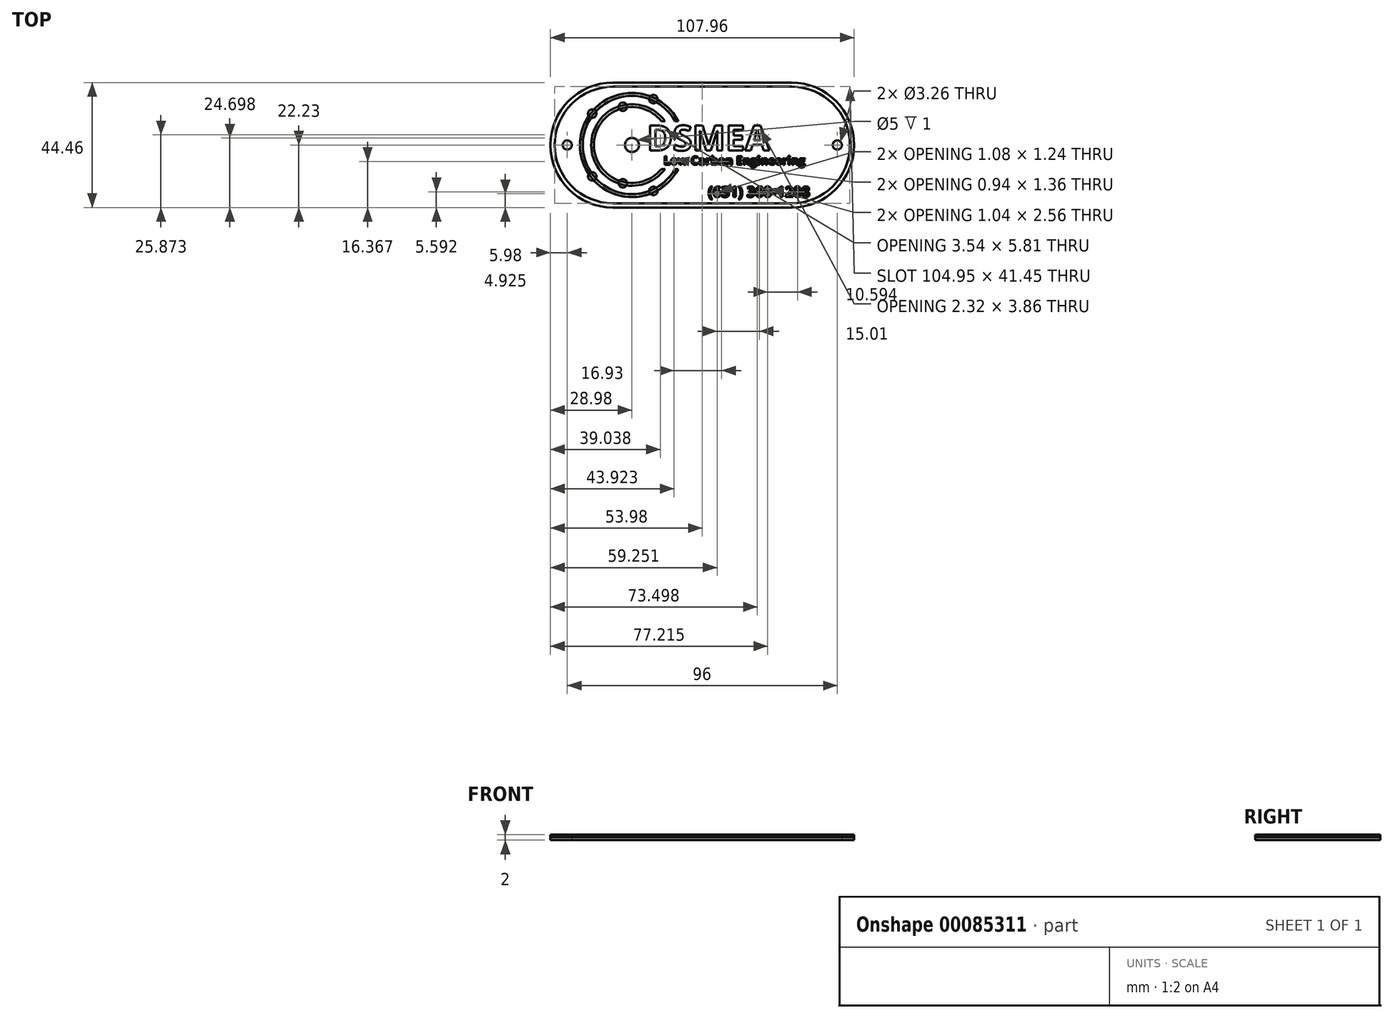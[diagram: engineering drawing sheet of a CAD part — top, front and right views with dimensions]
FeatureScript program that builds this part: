
annotation { "Feature Type Name" : "Feature", "Feature Type Description" : "" }
export const myFeature = defineFeature(function(context is Context, id is Id, definition is map)
    precondition{}
    {
        {
            var Q0;
            Q0=qCreatedBy(makeId("Top.planeOp"),FACE);
            var sketch = newSketch(context, id + "F0", { "sketchPlane" : qUnion([Q0])});
            skLineSegment(sketch, "E0.bottom", {"start": v(31.75, 22.22) * mm, "end": v(-31.75, 22.22) * mm});
            skLineSegment(sketch, "E0.top", {"start": v(31.75, -22.23) * mm, "end": v(-31.75, -22.23) * mm});
            skPoint(sketch, "E0.middle", {"position": v(0, 0) * mm});
            skArc(sketch, "E1", {"start": v(31.75, -22.23) * mm, "mid": v(53.98, 0) * mm, "end": v(31.75, 22.23) * mm});
            skArc(sketch, "E2", {"start": v(-31.75, 22.23) * mm, "mid": v(-53.98, 0) * mm, "end": v(-31.75, -22.23) * mm});
            skSolve(sketch);
        }
        {
            var Q0;
            Q0=qSketchRegion(id+"F0",true);
            extrude(context, id + "F1", {"entities" : qUnion([Q0]), "depth" : 2 * mm});
        }
        {
            var Q0;
            Q0=qCreatedBy(makeId("Top.planeOp"),FACE);
            cPlane(context, id + "F2", {"entities" : qUnion([Q0]), "cplaneType" : CPlaneType.OFFSET, "offset" : 1 * mm, "width" : 150 * mm, "height" : 150 * mm});
        }
        {
            var Q0;
            Q0=qCreatedBy(id+"F2.planeOp",FACE);
            var sketch = newSketch(context, id + "F3", { "sketchPlane" : qUnion([Q0])});
            skArc(sketch, "E3", {"start": v(-31.75, 22.23) * mm, "mid": v(-53.98, 0) * mm, "end": v(-31.75, -22.23) * mm});
            skArc(sketch, "E4.0", {"start": v(-31.75, 20.73) * mm, "mid": v(-52.48, 0) * mm, "end": v(-31.75, -20.73) * mm});
            skArc(sketch, "E5.MirrorC", {"start": v(31.75, 22.23) * mm, "mid": v(53.98, 0) * mm, "end": v(31.75, -22.23) * mm});
            skArc(sketch, "E6.MirrorC", {"start": v(31.75, 20.73) * mm, "mid": v(52.48, 0) * mm, "end": v(31.75, -20.73) * mm});
            skLineSegment(sketch, "E7", {"start": v(-31.75, -22.23) * mm, "end": v(31.75, -22.23) * mm});
            skLineSegment(sketch, "E8.MirrorCS", {"start": v(-31.75, 22.23) * mm, "end": v(31.75, 22.23) * mm});
            skLineSegment(sketch, "E9.0", {"start": v(-31.75, 20.73) * mm, "end": v(31.75, 20.73) * mm});
            skLineSegment(sketch, "E10.MirrorCS", {"start": v(-31.75, -20.73) * mm, "end": v(31.75, -20.73) * mm});
            skSolve(sketch);
        }
        {
            var Q0;
            Q0=qSketchRegion(id+"F3",true);
            extrude(context, id + "F4", {"entities" : qUnion([Q0]), "depth" : 1 * mm});
        }
        {
            var Q0;
            Q0=qCreatedBy(id+"F2.planeOp",FACE);
            var sketch = newSketch(context, id + "F5", { "sketchPlane" : qUnion([Q0])});
            skArc(sketch, "E11", {"start": v(-8.57, 8.5) * mm, "mid": v(-43.5, 0) * mm, "end": v(-8.57, -8.5) * mm});
            skArc(sketch, "E12", {"start": v(-9.7, 8.5) * mm, "mid": v(-42.5, 0) * mm, "end": v(-9.7, -8.5) * mm});
            skLineSegment(sketch, "E13.bottom", {"start": v(-8.57, 8.5) * mm, "end": v(-9.7, 8.5) * mm});
            skLineSegment(sketch, "E13.top", {"start": v(-8.57, -8.5) * mm, "end": v(-9.7, -8.5) * mm});
            skPoint(sketch, "E13.middle", {"position": v(0, 0) * mm});
            skSolve(sketch);
        }
        {
            var Q0;
            Q0=qSketchRegion(id+"F5",true);
            extrude(context, id + "F6", {"entities" : qUnion([Q0]), "depth" : 1 * mm});
        }
        {
            var Q0;
            Q0=qCreatedBy(id+"F2.planeOp",FACE);
            var sketch = newSketch(context, id + "F7", { "sketchPlane" : qUnion([Q0])});
            skArc(sketch, "E14", {"start": v(-13.25, 8.5) * mm, "mid": v(-39.5, 0) * mm, "end": v(-13.25, -8.5) * mm});
            skArc(sketch, "E15", {"start": v(-14.51, 8.5) * mm, "mid": v(-38.5, 0) * mm, "end": v(-14.51, -8.5) * mm});
            skLineSegment(sketch, "E16.bottom", {"start": v(-13.25, 8.5) * mm, "end": v(-14.51, 8.5) * mm});
            skLineSegment(sketch, "E16.top", {"start": v(-13.25, -8.5) * mm, "end": v(-14.51, -8.5) * mm});
            skPoint(sketch, "E16.middle", {"position": v(0, 0) * mm});
            skSolve(sketch);
        }
        {
            var Q0;
            Q0=qSketchRegion(id+"F7",true);
            extrude(context, id + "F8", {"entities" : qUnion([Q0]), "depth" : 1 * mm});
        }
        {
            var Q0;
            Q0=qCreatedBy(id+"F2.planeOp",FACE);
            var sketch = newSketch(context, id + "F9", { "sketchPlane" : qUnion([Q0])});
            skCircle(sketch, "E17", {"center": v(-25, 0) * mm, "radius": 2.5 * mm});
            skCircle(sketch, "E18", {"center": v(-17.4, 16.31) * mm, "radius": 1.5 * mm});
            skLineSegment(sketch, "E19.anchor1", {"start": v(-25, 0) * mm, "end": v(-17.4, 16.31) * mm, "construction": true});
            skLineSegment(sketch, "E19.anchor2", {"start": v(-25, 0) * mm, "end": v(-17.4, -16.31) * mm, "construction": true});
            skCircle(sketch, "E20", {"center": v(-28.23, 13.62) * mm, "radius": 1.5 * mm});
            skCircle(sketch, "E21.MirrorC", {"center": v(-28.23, -13.62) * mm, "radius": 1.5 * mm});
            skLineSegment(sketch, "E22", {"start": v(-59.58, 0) * mm, "end": v(0, 0) * mm, "construction": true});
            skCircle(sketch, "E23", {"center": v(-25, 0) * mm, "radius": 18 * mm, "construction": true});
            skCircle(sketch, "E24", {"center": v(-25, 0) * mm, "radius": 14 * mm, "construction": true});
            skLineSegment(sketch, "E25", {"start": v(-28.23, 13.62) * mm, "end": v(-35.98, 8.68) * mm, "construction": true});
            skLineSegment(sketch, "E26", {"start": v(-28.23, 13.62) * mm, "end": v(-19.08, 12.69) * mm, "construction": true});
            skCircle(sketch, "E27.1.0", {"center": v(-39.12, 11.16) * mm, "radius": 1.5 * mm});
            skCircle(sketch, "E27.2.0", {"center": v(-39.12, -11.16) * mm, "radius": 1.5 * mm});
            skCircle(sketch, "E27.3.0", {"center": v(-17.4, -16.31) * mm, "radius": 1.5 * mm});
            skSolve(sketch);
        }
        {
            var Q0;
            Q0=qSketchRegion(id+"F9",true);
            extrude(context, id + "F10", {"entities" : qUnion([Q0]), "depth" : 1 * mm});
        }
        {
            var Q0;
            Q0=qCreatedBy(id+"F2.planeOp",FACE);
            var sketch = newSketch(context, id + "F11", { "sketchPlane" : qUnion([Q0])});
            skText(sketch, "E28", { "text": "DSMEA", "fontName": "OpenSans-Bold.ttf"});
            const initialGuessF11  = {"E28": [-0.01973, -0.002, 1, 0, 0.009]};
            skSetInitialGuess(sketch, initialGuessF11);
            skSolve(sketch);
        }
        {
            var Q0;
            Q0=qSketchRegion(id+"F11",true);
            extrude(context, id + "F12", {"entities" : qUnion([Q0]), "depth" : 1 * mm});
        }
        {
            var Q0;
            Q0=qCreatedBy(id+"F2.planeOp",FACE);
            var sketch = newSketch(context, id + "F13", { "sketchPlane" : qUnion([Q0])});
            skText(sketch, "E29", { "text": "Low Carbon Engineering", "fontName": "OpenSans-Bold.ttf"});
            const initialGuessF13  = {"E29": [-0.0137, -0.007, 1, 0, 0.003]};
            skSetInitialGuess(sketch, initialGuessF13);
            skSolve(sketch);
        }
        {
            var Q0;
            Q0=qSketchRegion(id+"F13",true);
            extrude(context, id + "F14", {"entities" : qUnion([Q0]), "depth" : 1 * mm});
        }
        {
            var Q0;
            Q0=qCreatedBy(id+"F2.planeOp",FACE);
            var sketch = newSketch(context, id + "F15", { "sketchPlane" : qUnion([Q0])});
            skText(sketch, "E30", { "text": "(631) 360-1208", "fontName": "OpenSans-Bold.ttf"});
            const initialGuessF15  = {"E30": [0.002, -0.0185, 1, 0, 0.00375]};
            skSetInitialGuess(sketch, initialGuessF15);
            skSolve(sketch);
        }
        {
            var Q0;
            Q0=qSketchRegion(id+"F15",true);
            extrude(context, id + "F16", {"entities" : qUnion([Q0]), "depth" : 1 * mm});
        }
        {
            var Q0;
            Q0=makeQuery(id+"F6.opExtrude","SWEPT_BODY",BODY,{"disambiguationData":[OSD([sQuery(id+"F5.wireOp",EDGE,"E11"),sQuery(id+"F5.wireOp",EDGE,"E12")])]});
            var Q1;
            Q1=makeQuery(id+"F1.opExtrude","SWEPT_BODY",BODY,{"disambiguationData":[OSD([sQuery(id+"F0.wireOp",EDGE,"E0.bottom"),sQuery(id+"F0.wireOp",EDGE,"E0.top"),sQuery(id+"F0.wireOp",EDGE,"E1"),sQuery(id+"F0.wireOp",EDGE,"E2")])]});
            booleanBodies(context, id + "F17", {"operationType" : BooleanOperationType.SUBTRACTION, "tools" : qUnion([Q0]), "targets" : qUnion([Q1]), "keepTools" : true});
        }
        {
            var Q0;
            Q0=makeQuery(id+"F6.opExtrude","SWEPT_BODY",BODY,{"disambiguationData":[OSD([sQuery(id+"F5.wireOp",EDGE,"E11"),sQuery(id+"F5.wireOp",EDGE,"E12")])]});
            var Q1;
            Q1=makeQuery(id+"F10.opExtrude","SWEPT_BODY",BODY,{"disambiguationData":[OSD([sQuery(id+"F9.wireOp",EDGE,"E17")])]});
            var Q2;
            Q2=makeQuery(id+"F8.opExtrude","SWEPT_BODY",BODY,{"disambiguationData":[OSD([sQuery(id+"F7.wireOp",EDGE,"E14"),sQuery(id+"F7.wireOp",EDGE,"E15")])]});
            var Q3;
            Q3=makeQuery(id+"F1.opExtrude","SWEPT_BODY",BODY,{"disambiguationData":[OSD([sQuery(id+"F0.wireOp",EDGE,"E0.bottom"),sQuery(id+"F0.wireOp",EDGE,"E0.top"),sQuery(id+"F0.wireOp",EDGE,"E1"),sQuery(id+"F0.wireOp",EDGE,"E2")])]});
            booleanBodies(context, id + "F18", {"operationType" : BooleanOperationType.SUBTRACTION, "tools" : qUnion([Q0, Q1, Q2]), "targets" : qUnion([Q3]), "keepTools" : true});
        }
        {
            var Q0;
            Q0=makeQuery(id+"F12.opExtrude","SWEPT_BODY",BODY,{"disambiguationData":[OSD([sQuery(id+"F11.wireOp",EDGE,"E28.sketch_text.stroke-0"),sQuery(id+"F11.wireOp",EDGE,"E28.sketch_text.stroke-1"),sQuery(id+"F11.wireOp",EDGE,"E28.sketch_text.stroke-2"),sQuery(id+"F11.wireOp",EDGE,"E28.sketch_text.stroke-3"),sQuery(id+"F11.wireOp",EDGE,"E28.sketch_text.stroke-4"),sQuery(id+"F11.wireOp",EDGE,"E28.sketch_text.stroke-5"),sQuery(id+"F11.wireOp",EDGE,"E28.sketch_text.stroke-6"),sQuery(id+"F11.wireOp",EDGE,"E28.sketch_text.stroke-7"),sQuery(id+"F11.wireOp",EDGE,"E28.sketch_text.stroke-8"),sQuery(id+"F11.wireOp",EDGE,"E28.sketch_text.stroke-9"),sQuery(id+"F11.wireOp",EDGE,"E28.sketch_text.stroke-10"),sQuery(id+"F11.wireOp",EDGE,"E28.sketch_text.stroke-11")])]});
            var Q1;
            Q1=makeQuery(id+"F12.opExtrude","SWEPT_BODY",BODY,{"disambiguationData":[OSD([sQuery(id+"F11.wireOp",EDGE,"E28.sketch_text.stroke-12"),sQuery(id+"F11.wireOp",EDGE,"E28.sketch_text.stroke-13"),sQuery(id+"F11.wireOp",EDGE,"E28.sketch_text.stroke-14"),sQuery(id+"F11.wireOp",EDGE,"E28.sketch_text.stroke-15"),sQuery(id+"F11.wireOp",EDGE,"E28.sketch_text.stroke-16"),sQuery(id+"F11.wireOp",EDGE,"E28.sketch_text.stroke-17"),sQuery(id+"F11.wireOp",EDGE,"E28.sketch_text.stroke-18"),sQuery(id+"F11.wireOp",EDGE,"E28.sketch_text.stroke-19"),sQuery(id+"F11.wireOp",EDGE,"E28.sketch_text.stroke-20"),sQuery(id+"F11.wireOp",EDGE,"E28.sketch_text.stroke-21"),sQuery(id+"F11.wireOp",EDGE,"E28.sketch_text.stroke-22"),sQuery(id+"F11.wireOp",EDGE,"E28.sketch_text.stroke-23"),sQuery(id+"F11.wireOp",EDGE,"E28.sketch_text.stroke-24"),sQuery(id+"F11.wireOp",EDGE,"E28.sketch_text.stroke-25"),sQuery(id+"F11.wireOp",EDGE,"E28.sketch_text.stroke-26"),sQuery(id+"F11.wireOp",EDGE,"E28.sketch_text.stroke-27"),sQuery(id+"F11.wireOp",EDGE,"E28.sketch_text.stroke-28"),sQuery(id+"F11.wireOp",EDGE,"E28.sketch_text.stroke-29"),sQuery(id+"F11.wireOp",EDGE,"E28.sketch_text.stroke-30"),sQuery(id+"F11.wireOp",EDGE,"E28.sketch_text.stroke-31"),sQuery(id+"F11.wireOp",EDGE,"E28.sketch_text.stroke-32"),sQuery(id+"F11.wireOp",EDGE,"E28.sketch_text.stroke-33"),sQuery(id+"F11.wireOp",EDGE,"E28.sketch_text.stroke-34"),sQuery(id+"F11.wireOp",EDGE,"E28.sketch_text.stroke-35"),sQuery(id+"F11.wireOp",EDGE,"E28.sketch_text.stroke-36"),sQuery(id+"F11.wireOp",EDGE,"E28.sketch_text.stroke-37"),sQuery(id+"F11.wireOp",EDGE,"E28.sketch_text.stroke-38"),sQuery(id+"F11.wireOp",EDGE,"E28.sketch_text.stroke-39")])]});
            var Q2;
            Q2=makeQuery(id+"F12.opExtrude","SWEPT_BODY",BODY,{"disambiguationData":[OSD([sQuery(id+"F11.wireOp",EDGE,"E28.sketch_text.stroke-40"),sQuery(id+"F11.wireOp",EDGE,"E28.sketch_text.stroke-41"),sQuery(id+"F11.wireOp",EDGE,"E28.sketch_text.stroke-42"),sQuery(id+"F11.wireOp",EDGE,"E28.sketch_text.stroke-43"),sQuery(id+"F11.wireOp",EDGE,"E28.sketch_text.stroke-44"),sQuery(id+"F11.wireOp",EDGE,"E28.sketch_text.stroke-45"),sQuery(id+"F11.wireOp",EDGE,"E28.sketch_text.stroke-46"),sQuery(id+"F11.wireOp",EDGE,"E28.sketch_text.stroke-47"),sQuery(id+"F11.wireOp",EDGE,"E28.sketch_text.stroke-48"),sQuery(id+"F11.wireOp",EDGE,"E28.sketch_text.stroke-49"),sQuery(id+"F11.wireOp",EDGE,"E28.sketch_text.stroke-50"),sQuery(id+"F11.wireOp",EDGE,"E28.sketch_text.stroke-51"),sQuery(id+"F11.wireOp",EDGE,"E28.sketch_text.stroke-52"),sQuery(id+"F11.wireOp",EDGE,"E28.sketch_text.stroke-53"),sQuery(id+"F11.wireOp",EDGE,"E28.sketch_text.stroke-54"),sQuery(id+"F11.wireOp",EDGE,"E28.sketch_text.stroke-55"),sQuery(id+"F11.wireOp",EDGE,"E28.sketch_text.stroke-56"),sQuery(id+"F11.wireOp",EDGE,"E28.sketch_text.stroke-57"),sQuery(id+"F11.wireOp",EDGE,"E28.sketch_text.stroke-58")])]});
            var Q3;
            Q3=makeQuery(id+"F12.opExtrude","SWEPT_BODY",BODY,{"disambiguationData":[OSD([sQuery(id+"F11.wireOp",EDGE,"E28.sketch_text.stroke-59"),sQuery(id+"F11.wireOp",EDGE,"E28.sketch_text.stroke-60"),sQuery(id+"F11.wireOp",EDGE,"E28.sketch_text.stroke-61"),sQuery(id+"F11.wireOp",EDGE,"E28.sketch_text.stroke-62"),sQuery(id+"F11.wireOp",EDGE,"E28.sketch_text.stroke-63"),sQuery(id+"F11.wireOp",EDGE,"E28.sketch_text.stroke-64"),sQuery(id+"F11.wireOp",EDGE,"E28.sketch_text.stroke-65"),sQuery(id+"F11.wireOp",EDGE,"E28.sketch_text.stroke-66"),sQuery(id+"F11.wireOp",EDGE,"E28.sketch_text.stroke-67"),sQuery(id+"F11.wireOp",EDGE,"E28.sketch_text.stroke-68"),sQuery(id+"F11.wireOp",EDGE,"E28.sketch_text.stroke-69"),sQuery(id+"F11.wireOp",EDGE,"E28.sketch_text.stroke-70")])]});
            var Q4;
            Q4=makeQuery(id+"F12.opExtrude","SWEPT_BODY",BODY,{"disambiguationData":[OSD([sQuery(id+"F11.wireOp",EDGE,"E28.sketch_text.stroke-71"),sQuery(id+"F11.wireOp",EDGE,"E28.sketch_text.stroke-72"),sQuery(id+"F11.wireOp",EDGE,"E28.sketch_text.stroke-73"),sQuery(id+"F11.wireOp",EDGE,"E28.sketch_text.stroke-74"),sQuery(id+"F11.wireOp",EDGE,"E28.sketch_text.stroke-75"),sQuery(id+"F11.wireOp",EDGE,"E28.sketch_text.stroke-76"),sQuery(id+"F11.wireOp",EDGE,"E28.sketch_text.stroke-77"),sQuery(id+"F11.wireOp",EDGE,"E28.sketch_text.stroke-78"),sQuery(id+"F11.wireOp",EDGE,"E28.sketch_text.stroke-79"),sQuery(id+"F11.wireOp",EDGE,"E28.sketch_text.stroke-80"),sQuery(id+"F11.wireOp",EDGE,"E28.sketch_text.stroke-81"),sQuery(id+"F11.wireOp",EDGE,"E28.sketch_text.stroke-82")])]});
            var Q5;
            Q5=makeQuery(id+"F1.opExtrude","SWEPT_BODY",BODY,{"disambiguationData":[OSD([sQuery(id+"F0.wireOp",EDGE,"E0.bottom"),sQuery(id+"F0.wireOp",EDGE,"E0.top"),sQuery(id+"F0.wireOp",EDGE,"E1"),sQuery(id+"F0.wireOp",EDGE,"E2")])]});
            booleanBodies(context, id + "F19", {"operationType" : BooleanOperationType.SUBTRACTION, "tools" : qUnion([Q0, Q1, Q2, Q3, Q4]), "targets" : qUnion([Q5]), "keepTools" : true});
        }
        {
            var Q0;
            Q0=makeQuery(id+"F14.opExtrude","SWEPT_BODY",BODY,{"disambiguationData":[OSD([sQuery(id+"F13.wireOp",EDGE,"E29.sketch_text.stroke-0"),sQuery(id+"F13.wireOp",EDGE,"E29.sketch_text.stroke-1"),sQuery(id+"F13.wireOp",EDGE,"E29.sketch_text.stroke-2"),sQuery(id+"F13.wireOp",EDGE,"E29.sketch_text.stroke-3"),sQuery(id+"F13.wireOp",EDGE,"E29.sketch_text.stroke-4"),sQuery(id+"F13.wireOp",EDGE,"E29.sketch_text.stroke-5")])]});
            var Q1;
            Q1=makeQuery(id+"F14.opExtrude","SWEPT_BODY",BODY,{"disambiguationData":[OSD([sQuery(id+"F13.wireOp",EDGE,"E29.sketch_text.stroke-6"),sQuery(id+"F13.wireOp",EDGE,"E29.sketch_text.stroke-7"),sQuery(id+"F13.wireOp",EDGE,"E29.sketch_text.stroke-8"),sQuery(id+"F13.wireOp",EDGE,"E29.sketch_text.stroke-9"),sQuery(id+"F13.wireOp",EDGE,"E29.sketch_text.stroke-10"),sQuery(id+"F13.wireOp",EDGE,"E29.sketch_text.stroke-11"),sQuery(id+"F13.wireOp",EDGE,"E29.sketch_text.stroke-12"),sQuery(id+"F13.wireOp",EDGE,"E29.sketch_text.stroke-13"),sQuery(id+"F13.wireOp",EDGE,"E29.sketch_text.stroke-14"),sQuery(id+"F13.wireOp",EDGE,"E29.sketch_text.stroke-15"),sQuery(id+"F13.wireOp",EDGE,"E29.sketch_text.stroke-16"),sQuery(id+"F13.wireOp",EDGE,"E29.sketch_text.stroke-17"),sQuery(id+"F13.wireOp",EDGE,"E29.sketch_text.stroke-18"),sQuery(id+"F13.wireOp",EDGE,"E29.sketch_text.stroke-19"),sQuery(id+"F13.wireOp",EDGE,"E29.sketch_text.stroke-20"),sQuery(id+"F13.wireOp",EDGE,"E29.sketch_text.stroke-21"),sQuery(id+"F13.wireOp",EDGE,"E29.sketch_text.stroke-22"),sQuery(id+"F13.wireOp",EDGE,"E29.sketch_text.stroke-23")])]});
            var Q2;
            Q2=makeQuery(id+"F14.opExtrude","SWEPT_BODY",BODY,{"disambiguationData":[OSD([sQuery(id+"F13.wireOp",EDGE,"E29.sketch_text.stroke-24"),sQuery(id+"F13.wireOp",EDGE,"E29.sketch_text.stroke-25"),sQuery(id+"F13.wireOp",EDGE,"E29.sketch_text.stroke-26"),sQuery(id+"F13.wireOp",EDGE,"E29.sketch_text.stroke-27"),sQuery(id+"F13.wireOp",EDGE,"E29.sketch_text.stroke-28"),sQuery(id+"F13.wireOp",EDGE,"E29.sketch_text.stroke-29"),sQuery(id+"F13.wireOp",EDGE,"E29.sketch_text.stroke-30"),sQuery(id+"F13.wireOp",EDGE,"E29.sketch_text.stroke-31"),sQuery(id+"F13.wireOp",EDGE,"E29.sketch_text.stroke-32"),sQuery(id+"F13.wireOp",EDGE,"E29.sketch_text.stroke-33"),sQuery(id+"F13.wireOp",EDGE,"E29.sketch_text.stroke-34"),sQuery(id+"F13.wireOp",EDGE,"E29.sketch_text.stroke-35"),sQuery(id+"F13.wireOp",EDGE,"E29.sketch_text.stroke-36"),sQuery(id+"F13.wireOp",EDGE,"E29.sketch_text.stroke-37"),sQuery(id+"F13.wireOp",EDGE,"E29.sketch_text.stroke-38"),sQuery(id+"F13.wireOp",EDGE,"E29.sketch_text.stroke-39"),sQuery(id+"F13.wireOp",EDGE,"E29.sketch_text.stroke-40"),sQuery(id+"F13.wireOp",EDGE,"E29.sketch_text.stroke-41"),sQuery(id+"F13.wireOp",EDGE,"E29.sketch_text.stroke-42"),sQuery(id+"F13.wireOp",EDGE,"E29.sketch_text.stroke-43"),sQuery(id+"F13.wireOp",EDGE,"E29.sketch_text.stroke-44"),sQuery(id+"F13.wireOp",EDGE,"E29.sketch_text.stroke-45"),sQuery(id+"F13.wireOp",EDGE,"E29.sketch_text.stroke-46"),sQuery(id+"F13.wireOp",EDGE,"E29.sketch_text.stroke-47"),sQuery(id+"F13.wireOp",EDGE,"E29.sketch_text.stroke-48"),sQuery(id+"F13.wireOp",EDGE,"E29.sketch_text.stroke-49")])]});
            var Q3;
            Q3=makeQuery(id+"F14.opExtrude","SWEPT_BODY",BODY,{"disambiguationData":[OSD([sQuery(id+"F13.wireOp",EDGE,"E29.sketch_text.stroke-50"),sQuery(id+"F13.wireOp",EDGE,"E29.sketch_text.stroke-51"),sQuery(id+"F13.wireOp",EDGE,"E29.sketch_text.stroke-52"),sQuery(id+"F13.wireOp",EDGE,"E29.sketch_text.stroke-53"),sQuery(id+"F13.wireOp",EDGE,"E29.sketch_text.stroke-54"),sQuery(id+"F13.wireOp",EDGE,"E29.sketch_text.stroke-55"),sQuery(id+"F13.wireOp",EDGE,"E29.sketch_text.stroke-56"),sQuery(id+"F13.wireOp",EDGE,"E29.sketch_text.stroke-57"),sQuery(id+"F13.wireOp",EDGE,"E29.sketch_text.stroke-58"),sQuery(id+"F13.wireOp",EDGE,"E29.sketch_text.stroke-59"),sQuery(id+"F13.wireOp",EDGE,"E29.sketch_text.stroke-60"),sQuery(id+"F13.wireOp",EDGE,"E29.sketch_text.stroke-61"),sQuery(id+"F13.wireOp",EDGE,"E29.sketch_text.stroke-62"),sQuery(id+"F13.wireOp",EDGE,"E29.sketch_text.stroke-63"),sQuery(id+"F13.wireOp",EDGE,"E29.sketch_text.stroke-64")])]});
            var Q4;
            Q4=makeQuery(id+"F14.opExtrude","SWEPT_BODY",BODY,{"disambiguationData":[OSD([sQuery(id+"F13.wireOp",EDGE,"E29.sketch_text.stroke-65"),sQuery(id+"F13.wireOp",EDGE,"E29.sketch_text.stroke-66"),sQuery(id+"F13.wireOp",EDGE,"E29.sketch_text.stroke-67"),sQuery(id+"F13.wireOp",EDGE,"E29.sketch_text.stroke-68"),sQuery(id+"F13.wireOp",EDGE,"E29.sketch_text.stroke-69"),sQuery(id+"F13.wireOp",EDGE,"E29.sketch_text.stroke-70"),sQuery(id+"F13.wireOp",EDGE,"E29.sketch_text.stroke-71"),sQuery(id+"F13.wireOp",EDGE,"E29.sketch_text.stroke-72"),sQuery(id+"F13.wireOp",EDGE,"E29.sketch_text.stroke-73"),sQuery(id+"F13.wireOp",EDGE,"E29.sketch_text.stroke-74"),sQuery(id+"F13.wireOp",EDGE,"E29.sketch_text.stroke-75"),sQuery(id+"F13.wireOp",EDGE,"E29.sketch_text.stroke-76"),sQuery(id+"F13.wireOp",EDGE,"E29.sketch_text.stroke-77"),sQuery(id+"F13.wireOp",EDGE,"E29.sketch_text.stroke-78"),sQuery(id+"F13.wireOp",EDGE,"E29.sketch_text.stroke-79"),sQuery(id+"F13.wireOp",EDGE,"E29.sketch_text.stroke-80"),sQuery(id+"F13.wireOp",EDGE,"E29.sketch_text.stroke-81"),sQuery(id+"F13.wireOp",EDGE,"E29.sketch_text.stroke-82"),sQuery(id+"F13.wireOp",EDGE,"E29.sketch_text.stroke-83"),sQuery(id+"F13.wireOp",EDGE,"E29.sketch_text.stroke-84"),sQuery(id+"F13.wireOp",EDGE,"E29.sketch_text.stroke-85"),sQuery(id+"F13.wireOp",EDGE,"E29.sketch_text.stroke-86"),sQuery(id+"F13.wireOp",EDGE,"E29.sketch_text.stroke-87"),sQuery(id+"F13.wireOp",EDGE,"E29.sketch_text.stroke-88"),sQuery(id+"F13.wireOp",EDGE,"E29.sketch_text.stroke-89")])]});
            var Q5;
            Q5=makeQuery(id+"F14.opExtrude","SWEPT_BODY",BODY,{"disambiguationData":[OSD([sQuery(id+"F13.wireOp",EDGE,"E29.sketch_text.stroke-90"),sQuery(id+"F13.wireOp",EDGE,"E29.sketch_text.stroke-91"),sQuery(id+"F13.wireOp",EDGE,"E29.sketch_text.stroke-92"),sQuery(id+"F13.wireOp",EDGE,"E29.sketch_text.stroke-93"),sQuery(id+"F13.wireOp",EDGE,"E29.sketch_text.stroke-94"),sQuery(id+"F13.wireOp",EDGE,"E29.sketch_text.stroke-95"),sQuery(id+"F13.wireOp",EDGE,"E29.sketch_text.stroke-96"),sQuery(id+"F13.wireOp",EDGE,"E29.sketch_text.stroke-97"),sQuery(id+"F13.wireOp",EDGE,"E29.sketch_text.stroke-98"),sQuery(id+"F13.wireOp",EDGE,"E29.sketch_text.stroke-99"),sQuery(id+"F13.wireOp",EDGE,"E29.sketch_text.stroke-100"),sQuery(id+"F13.wireOp",EDGE,"E29.sketch_text.stroke-101"),sQuery(id+"F13.wireOp",EDGE,"E29.sketch_text.stroke-102")])]});
            var Q6;
            Q6=makeQuery(id+"F14.opExtrude","SWEPT_BODY",BODY,{"disambiguationData":[OSD([sQuery(id+"F13.wireOp",EDGE,"E29.sketch_text.stroke-103"),sQuery(id+"F13.wireOp",EDGE,"E29.sketch_text.stroke-104"),sQuery(id+"F13.wireOp",EDGE,"E29.sketch_text.stroke-105"),sQuery(id+"F13.wireOp",EDGE,"E29.sketch_text.stroke-106"),sQuery(id+"F13.wireOp",EDGE,"E29.sketch_text.stroke-107"),sQuery(id+"F13.wireOp",EDGE,"E29.sketch_text.stroke-108"),sQuery(id+"F13.wireOp",EDGE,"E29.sketch_text.stroke-109"),sQuery(id+"F13.wireOp",EDGE,"E29.sketch_text.stroke-110"),sQuery(id+"F13.wireOp",EDGE,"E29.sketch_text.stroke-111"),sQuery(id+"F13.wireOp",EDGE,"E29.sketch_text.stroke-112"),sQuery(id+"F13.wireOp",EDGE,"E29.sketch_text.stroke-113"),sQuery(id+"F13.wireOp",EDGE,"E29.sketch_text.stroke-114"),sQuery(id+"F13.wireOp",EDGE,"E29.sketch_text.stroke-115"),sQuery(id+"F13.wireOp",EDGE,"E29.sketch_text.stroke-116"),sQuery(id+"F13.wireOp",EDGE,"E29.sketch_text.stroke-117"),sQuery(id+"F13.wireOp",EDGE,"E29.sketch_text.stroke-118"),sQuery(id+"F13.wireOp",EDGE,"E29.sketch_text.stroke-119"),sQuery(id+"F13.wireOp",EDGE,"E29.sketch_text.stroke-120"),sQuery(id+"F13.wireOp",EDGE,"E29.sketch_text.stroke-121"),sQuery(id+"F13.wireOp",EDGE,"E29.sketch_text.stroke-122"),sQuery(id+"F13.wireOp",EDGE,"E29.sketch_text.stroke-123"),sQuery(id+"F13.wireOp",EDGE,"E29.sketch_text.stroke-124"),sQuery(id+"F13.wireOp",EDGE,"E29.sketch_text.stroke-125")])]});
            var Q7;
            Q7=makeQuery(id+"F14.opExtrude","SWEPT_BODY",BODY,{"disambiguationData":[OSD([sQuery(id+"F13.wireOp",EDGE,"E29.sketch_text.stroke-126"),sQuery(id+"F13.wireOp",EDGE,"E29.sketch_text.stroke-127"),sQuery(id+"F13.wireOp",EDGE,"E29.sketch_text.stroke-128"),sQuery(id+"F13.wireOp",EDGE,"E29.sketch_text.stroke-129"),sQuery(id+"F13.wireOp",EDGE,"E29.sketch_text.stroke-130"),sQuery(id+"F13.wireOp",EDGE,"E29.sketch_text.stroke-131"),sQuery(id+"F13.wireOp",EDGE,"E29.sketch_text.stroke-132"),sQuery(id+"F13.wireOp",EDGE,"E29.sketch_text.stroke-133"),sQuery(id+"F13.wireOp",EDGE,"E29.sketch_text.stroke-134"),sQuery(id+"F13.wireOp",EDGE,"E29.sketch_text.stroke-135"),sQuery(id+"F13.wireOp",EDGE,"E29.sketch_text.stroke-136"),sQuery(id+"F13.wireOp",EDGE,"E29.sketch_text.stroke-137"),sQuery(id+"F13.wireOp",EDGE,"E29.sketch_text.stroke-138"),sQuery(id+"F13.wireOp",EDGE,"E29.sketch_text.stroke-139"),sQuery(id+"F13.wireOp",EDGE,"E29.sketch_text.stroke-140"),sQuery(id+"F13.wireOp",EDGE,"E29.sketch_text.stroke-141"),sQuery(id+"F13.wireOp",EDGE,"E29.sketch_text.stroke-142"),sQuery(id+"F13.wireOp",EDGE,"E29.sketch_text.stroke-143")])]});
            var Q8;
            Q8=makeQuery(id+"F14.opExtrude","SWEPT_BODY",BODY,{"disambiguationData":[OSD([sQuery(id+"F13.wireOp",EDGE,"E29.sketch_text.stroke-144"),sQuery(id+"F13.wireOp",EDGE,"E29.sketch_text.stroke-145"),sQuery(id+"F13.wireOp",EDGE,"E29.sketch_text.stroke-146"),sQuery(id+"F13.wireOp",EDGE,"E29.sketch_text.stroke-147"),sQuery(id+"F13.wireOp",EDGE,"E29.sketch_text.stroke-148"),sQuery(id+"F13.wireOp",EDGE,"E29.sketch_text.stroke-149"),sQuery(id+"F13.wireOp",EDGE,"E29.sketch_text.stroke-150"),sQuery(id+"F13.wireOp",EDGE,"E29.sketch_text.stroke-151"),sQuery(id+"F13.wireOp",EDGE,"E29.sketch_text.stroke-152"),sQuery(id+"F13.wireOp",EDGE,"E29.sketch_text.stroke-153"),sQuery(id+"F13.wireOp",EDGE,"E29.sketch_text.stroke-154"),sQuery(id+"F13.wireOp",EDGE,"E29.sketch_text.stroke-155"),sQuery(id+"F13.wireOp",EDGE,"E29.sketch_text.stroke-156"),sQuery(id+"F13.wireOp",EDGE,"E29.sketch_text.stroke-157"),sQuery(id+"F13.wireOp",EDGE,"E29.sketch_text.stroke-158"),sQuery(id+"F13.wireOp",EDGE,"E29.sketch_text.stroke-159"),sQuery(id+"F13.wireOp",EDGE,"E29.sketch_text.stroke-160")])]});
            var Q9;
            Q9=makeQuery(id+"F14.opExtrude","SWEPT_BODY",BODY,{"disambiguationData":[OSD([sQuery(id+"F13.wireOp",EDGE,"E29.sketch_text.stroke-161"),sQuery(id+"F13.wireOp",EDGE,"E29.sketch_text.stroke-162"),sQuery(id+"F13.wireOp",EDGE,"E29.sketch_text.stroke-163"),sQuery(id+"F13.wireOp",EDGE,"E29.sketch_text.stroke-164"),sQuery(id+"F13.wireOp",EDGE,"E29.sketch_text.stroke-165"),sQuery(id+"F13.wireOp",EDGE,"E29.sketch_text.stroke-166"),sQuery(id+"F13.wireOp",EDGE,"E29.sketch_text.stroke-167"),sQuery(id+"F13.wireOp",EDGE,"E29.sketch_text.stroke-168"),sQuery(id+"F13.wireOp",EDGE,"E29.sketch_text.stroke-169"),sQuery(id+"F13.wireOp",EDGE,"E29.sketch_text.stroke-170"),sQuery(id+"F13.wireOp",EDGE,"E29.sketch_text.stroke-171"),sQuery(id+"F13.wireOp",EDGE,"E29.sketch_text.stroke-172")])]});
            var Q10;
            Q10=makeQuery(id+"F14.opExtrude","SWEPT_BODY",BODY,{"disambiguationData":[OSD([sQuery(id+"F13.wireOp",EDGE,"E29.sketch_text.stroke-173"),sQuery(id+"F13.wireOp",EDGE,"E29.sketch_text.stroke-174"),sQuery(id+"F13.wireOp",EDGE,"E29.sketch_text.stroke-175"),sQuery(id+"F13.wireOp",EDGE,"E29.sketch_text.stroke-176"),sQuery(id+"F13.wireOp",EDGE,"E29.sketch_text.stroke-177"),sQuery(id+"F13.wireOp",EDGE,"E29.sketch_text.stroke-178"),sQuery(id+"F13.wireOp",EDGE,"E29.sketch_text.stroke-179"),sQuery(id+"F13.wireOp",EDGE,"E29.sketch_text.stroke-180"),sQuery(id+"F13.wireOp",EDGE,"E29.sketch_text.stroke-181"),sQuery(id+"F13.wireOp",EDGE,"E29.sketch_text.stroke-182"),sQuery(id+"F13.wireOp",EDGE,"E29.sketch_text.stroke-183"),sQuery(id+"F13.wireOp",EDGE,"E29.sketch_text.stroke-184"),sQuery(id+"F13.wireOp",EDGE,"E29.sketch_text.stroke-185"),sQuery(id+"F13.wireOp",EDGE,"E29.sketch_text.stroke-186"),sQuery(id+"F13.wireOp",EDGE,"E29.sketch_text.stroke-187"),sQuery(id+"F13.wireOp",EDGE,"E29.sketch_text.stroke-188"),sQuery(id+"F13.wireOp",EDGE,"E29.sketch_text.stroke-189")])]});
            var Q11;
            Q11=makeQuery(id+"F14.opExtrude","SWEPT_BODY",BODY,{"disambiguationData":[OSD([sQuery(id+"F13.wireOp",EDGE,"E29.sketch_text.stroke-190"),sQuery(id+"F13.wireOp",EDGE,"E29.sketch_text.stroke-191"),sQuery(id+"F13.wireOp",EDGE,"E29.sketch_text.stroke-192"),sQuery(id+"F13.wireOp",EDGE,"E29.sketch_text.stroke-193"),sQuery(id+"F13.wireOp",EDGE,"E29.sketch_text.stroke-194"),sQuery(id+"F13.wireOp",EDGE,"E29.sketch_text.stroke-195"),sQuery(id+"F13.wireOp",EDGE,"E29.sketch_text.stroke-196"),sQuery(id+"F13.wireOp",EDGE,"E29.sketch_text.stroke-197"),sQuery(id+"F13.wireOp",EDGE,"E29.sketch_text.stroke-198"),sQuery(id+"F13.wireOp",EDGE,"E29.sketch_text.stroke-199"),sQuery(id+"F13.wireOp",EDGE,"E29.sketch_text.stroke-200"),sQuery(id+"F13.wireOp",EDGE,"E29.sketch_text.stroke-201"),sQuery(id+"F13.wireOp",EDGE,"E29.sketch_text.stroke-202"),sQuery(id+"F13.wireOp",EDGE,"E29.sketch_text.stroke-203"),sQuery(id+"F13.wireOp",EDGE,"E29.sketch_text.stroke-204"),sQuery(id+"F13.wireOp",EDGE,"E29.sketch_text.stroke-205"),sQuery(id+"F13.wireOp",EDGE,"E29.sketch_text.stroke-206"),sQuery(id+"F13.wireOp",EDGE,"E29.sketch_text.stroke-207"),sQuery(id+"F13.wireOp",EDGE,"E29.sketch_text.stroke-208"),sQuery(id+"F13.wireOp",EDGE,"E29.sketch_text.stroke-209"),sQuery(id+"F13.wireOp",EDGE,"E29.sketch_text.stroke-210"),sQuery(id+"F13.wireOp",EDGE,"E29.sketch_text.stroke-211"),sQuery(id+"F13.wireOp",EDGE,"E29.sketch_text.stroke-212"),sQuery(id+"F13.wireOp",EDGE,"E29.sketch_text.stroke-213"),sQuery(id+"F13.wireOp",EDGE,"E29.sketch_text.stroke-214"),sQuery(id+"F13.wireOp",EDGE,"E29.sketch_text.stroke-215"),sQuery(id+"F13.wireOp",EDGE,"E29.sketch_text.stroke-216"),sQuery(id+"F13.wireOp",EDGE,"E29.sketch_text.stroke-217"),sQuery(id+"F13.wireOp",EDGE,"E29.sketch_text.stroke-218"),sQuery(id+"F13.wireOp",EDGE,"E29.sketch_text.stroke-219"),sQuery(id+"F13.wireOp",EDGE,"E29.sketch_text.stroke-220"),sQuery(id+"F13.wireOp",EDGE,"E29.sketch_text.stroke-221"),sQuery(id+"F13.wireOp",EDGE,"E29.sketch_text.stroke-222"),sQuery(id+"F13.wireOp",EDGE,"E29.sketch_text.stroke-223"),sQuery(id+"F13.wireOp",EDGE,"E29.sketch_text.stroke-224"),sQuery(id+"F13.wireOp",EDGE,"E29.sketch_text.stroke-225"),sQuery(id+"F13.wireOp",EDGE,"E29.sketch_text.stroke-226"),sQuery(id+"F13.wireOp",EDGE,"E29.sketch_text.stroke-227"),sQuery(id+"F13.wireOp",EDGE,"E29.sketch_text.stroke-228"),sQuery(id+"F13.wireOp",EDGE,"E29.sketch_text.stroke-229"),sQuery(id+"F13.wireOp",EDGE,"E29.sketch_text.stroke-230"),sQuery(id+"F13.wireOp",EDGE,"E29.sketch_text.stroke-231"),sQuery(id+"F13.wireOp",EDGE,"E29.sketch_text.stroke-232"),sQuery(id+"F13.wireOp",EDGE,"E29.sketch_text.stroke-233")])]});
            var Q12;
            Q12=makeQuery(id+"F14.opExtrude","SWEPT_BODY",BODY,{"disambiguationData":[OSD([sQuery(id+"F13.wireOp",EDGE,"E29.sketch_text.stroke-234"),sQuery(id+"F13.wireOp",EDGE,"E29.sketch_text.stroke-235"),sQuery(id+"F13.wireOp",EDGE,"E29.sketch_text.stroke-236"),sQuery(id+"F13.wireOp",EDGE,"E29.sketch_text.stroke-237"),sQuery(id+"F13.wireOp",EDGE,"E29.sketch_text.stroke-238")])]});
            var Q13;
            Q13=makeQuery(id+"F14.opExtrude","SWEPT_BODY",BODY,{"disambiguationData":[OSD([sQuery(id+"F13.wireOp",EDGE,"E29.sketch_text.stroke-239"),sQuery(id+"F13.wireOp",EDGE,"E29.sketch_text.stroke-240"),sQuery(id+"F13.wireOp",EDGE,"E29.sketch_text.stroke-241"),sQuery(id+"F13.wireOp",EDGE,"E29.sketch_text.stroke-242")])]});
            var Q14;
            Q14=makeQuery(id+"F14.opExtrude","SWEPT_BODY",BODY,{"disambiguationData":[OSD([sQuery(id+"F13.wireOp",EDGE,"E29.sketch_text.stroke-243"),sQuery(id+"F13.wireOp",EDGE,"E29.sketch_text.stroke-244"),sQuery(id+"F13.wireOp",EDGE,"E29.sketch_text.stroke-245"),sQuery(id+"F13.wireOp",EDGE,"E29.sketch_text.stroke-246"),sQuery(id+"F13.wireOp",EDGE,"E29.sketch_text.stroke-247"),sQuery(id+"F13.wireOp",EDGE,"E29.sketch_text.stroke-248"),sQuery(id+"F13.wireOp",EDGE,"E29.sketch_text.stroke-249"),sQuery(id+"F13.wireOp",EDGE,"E29.sketch_text.stroke-250"),sQuery(id+"F13.wireOp",EDGE,"E29.sketch_text.stroke-251"),sQuery(id+"F13.wireOp",EDGE,"E29.sketch_text.stroke-252"),sQuery(id+"F13.wireOp",EDGE,"E29.sketch_text.stroke-253"),sQuery(id+"F13.wireOp",EDGE,"E29.sketch_text.stroke-254"),sQuery(id+"F13.wireOp",EDGE,"E29.sketch_text.stroke-255"),sQuery(id+"F13.wireOp",EDGE,"E29.sketch_text.stroke-256"),sQuery(id+"F13.wireOp",EDGE,"E29.sketch_text.stroke-257"),sQuery(id+"F13.wireOp",EDGE,"E29.sketch_text.stroke-258"),sQuery(id+"F13.wireOp",EDGE,"E29.sketch_text.stroke-259")])]});
            var Q15;
            Q15=makeQuery(id+"F14.opExtrude","SWEPT_BODY",BODY,{"disambiguationData":[OSD([sQuery(id+"F13.wireOp",EDGE,"E29.sketch_text.stroke-260"),sQuery(id+"F13.wireOp",EDGE,"E29.sketch_text.stroke-261"),sQuery(id+"F13.wireOp",EDGE,"E29.sketch_text.stroke-262"),sQuery(id+"F13.wireOp",EDGE,"E29.sketch_text.stroke-263"),sQuery(id+"F13.wireOp",EDGE,"E29.sketch_text.stroke-264"),sQuery(id+"F13.wireOp",EDGE,"E29.sketch_text.stroke-265"),sQuery(id+"F13.wireOp",EDGE,"E29.sketch_text.stroke-266"),sQuery(id+"F13.wireOp",EDGE,"E29.sketch_text.stroke-267"),sQuery(id+"F13.wireOp",EDGE,"E29.sketch_text.stroke-268"),sQuery(id+"F13.wireOp",EDGE,"E29.sketch_text.stroke-269"),sQuery(id+"F13.wireOp",EDGE,"E29.sketch_text.stroke-270"),sQuery(id+"F13.wireOp",EDGE,"E29.sketch_text.stroke-271"),sQuery(id+"F13.wireOp",EDGE,"E29.sketch_text.stroke-272"),sQuery(id+"F13.wireOp",EDGE,"E29.sketch_text.stroke-273"),sQuery(id+"F13.wireOp",EDGE,"E29.sketch_text.stroke-274"),sQuery(id+"F13.wireOp",EDGE,"E29.sketch_text.stroke-275"),sQuery(id+"F13.wireOp",EDGE,"E29.sketch_text.stroke-276"),sQuery(id+"F13.wireOp",EDGE,"E29.sketch_text.stroke-277"),sQuery(id+"F13.wireOp",EDGE,"E29.sketch_text.stroke-278"),sQuery(id+"F13.wireOp",EDGE,"E29.sketch_text.stroke-279")])]});
            var Q16;
            Q16=makeQuery(id+"F14.opExtrude","SWEPT_BODY",BODY,{"disambiguationData":[OSD([sQuery(id+"F13.wireOp",EDGE,"E29.sketch_text.stroke-280"),sQuery(id+"F13.wireOp",EDGE,"E29.sketch_text.stroke-281"),sQuery(id+"F13.wireOp",EDGE,"E29.sketch_text.stroke-282"),sQuery(id+"F13.wireOp",EDGE,"E29.sketch_text.stroke-283"),sQuery(id+"F13.wireOp",EDGE,"E29.sketch_text.stroke-284"),sQuery(id+"F13.wireOp",EDGE,"E29.sketch_text.stroke-285"),sQuery(id+"F13.wireOp",EDGE,"E29.sketch_text.stroke-286"),sQuery(id+"F13.wireOp",EDGE,"E29.sketch_text.stroke-287"),sQuery(id+"F13.wireOp",EDGE,"E29.sketch_text.stroke-288"),sQuery(id+"F13.wireOp",EDGE,"E29.sketch_text.stroke-289"),sQuery(id+"F13.wireOp",EDGE,"E29.sketch_text.stroke-290"),sQuery(id+"F13.wireOp",EDGE,"E29.sketch_text.stroke-291"),sQuery(id+"F13.wireOp",EDGE,"E29.sketch_text.stroke-292"),sQuery(id+"F13.wireOp",EDGE,"E29.sketch_text.stroke-293"),sQuery(id+"F13.wireOp",EDGE,"E29.sketch_text.stroke-294"),sQuery(id+"F13.wireOp",EDGE,"E29.sketch_text.stroke-295"),sQuery(id+"F13.wireOp",EDGE,"E29.sketch_text.stroke-296"),sQuery(id+"F13.wireOp",EDGE,"E29.sketch_text.stroke-297"),sQuery(id+"F13.wireOp",EDGE,"E29.sketch_text.stroke-298"),sQuery(id+"F13.wireOp",EDGE,"E29.sketch_text.stroke-299")])]});
            var Q17;
            Q17=makeQuery(id+"F14.opExtrude","SWEPT_BODY",BODY,{"disambiguationData":[OSD([sQuery(id+"F13.wireOp",EDGE,"E29.sketch_text.stroke-300"),sQuery(id+"F13.wireOp",EDGE,"E29.sketch_text.stroke-301"),sQuery(id+"F13.wireOp",EDGE,"E29.sketch_text.stroke-302"),sQuery(id+"F13.wireOp",EDGE,"E29.sketch_text.stroke-303"),sQuery(id+"F13.wireOp",EDGE,"E29.sketch_text.stroke-304"),sQuery(id+"F13.wireOp",EDGE,"E29.sketch_text.stroke-305"),sQuery(id+"F13.wireOp",EDGE,"E29.sketch_text.stroke-306"),sQuery(id+"F13.wireOp",EDGE,"E29.sketch_text.stroke-307"),sQuery(id+"F13.wireOp",EDGE,"E29.sketch_text.stroke-308"),sQuery(id+"F13.wireOp",EDGE,"E29.sketch_text.stroke-309"),sQuery(id+"F13.wireOp",EDGE,"E29.sketch_text.stroke-310"),sQuery(id+"F13.wireOp",EDGE,"E29.sketch_text.stroke-311"),sQuery(id+"F13.wireOp",EDGE,"E29.sketch_text.stroke-312")])]});
            var Q18;
            Q18=makeQuery(id+"F14.opExtrude","SWEPT_BODY",BODY,{"disambiguationData":[OSD([sQuery(id+"F13.wireOp",EDGE,"E29.sketch_text.stroke-313"),sQuery(id+"F13.wireOp",EDGE,"E29.sketch_text.stroke-314"),sQuery(id+"F13.wireOp",EDGE,"E29.sketch_text.stroke-315"),sQuery(id+"F13.wireOp",EDGE,"E29.sketch_text.stroke-316"),sQuery(id+"F13.wireOp",EDGE,"E29.sketch_text.stroke-317")])]});
            var Q19;
            Q19=makeQuery(id+"F14.opExtrude","SWEPT_BODY",BODY,{"disambiguationData":[OSD([sQuery(id+"F13.wireOp",EDGE,"E29.sketch_text.stroke-318"),sQuery(id+"F13.wireOp",EDGE,"E29.sketch_text.stroke-319"),sQuery(id+"F13.wireOp",EDGE,"E29.sketch_text.stroke-320"),sQuery(id+"F13.wireOp",EDGE,"E29.sketch_text.stroke-321")])]});
            var Q20;
            Q20=makeQuery(id+"F14.opExtrude","SWEPT_BODY",BODY,{"disambiguationData":[OSD([sQuery(id+"F13.wireOp",EDGE,"E29.sketch_text.stroke-322"),sQuery(id+"F13.wireOp",EDGE,"E29.sketch_text.stroke-323"),sQuery(id+"F13.wireOp",EDGE,"E29.sketch_text.stroke-324"),sQuery(id+"F13.wireOp",EDGE,"E29.sketch_text.stroke-325"),sQuery(id+"F13.wireOp",EDGE,"E29.sketch_text.stroke-326"),sQuery(id+"F13.wireOp",EDGE,"E29.sketch_text.stroke-327"),sQuery(id+"F13.wireOp",EDGE,"E29.sketch_text.stroke-328"),sQuery(id+"F13.wireOp",EDGE,"E29.sketch_text.stroke-329"),sQuery(id+"F13.wireOp",EDGE,"E29.sketch_text.stroke-330"),sQuery(id+"F13.wireOp",EDGE,"E29.sketch_text.stroke-331"),sQuery(id+"F13.wireOp",EDGE,"E29.sketch_text.stroke-332"),sQuery(id+"F13.wireOp",EDGE,"E29.sketch_text.stroke-333"),sQuery(id+"F13.wireOp",EDGE,"E29.sketch_text.stroke-334"),sQuery(id+"F13.wireOp",EDGE,"E29.sketch_text.stroke-335"),sQuery(id+"F13.wireOp",EDGE,"E29.sketch_text.stroke-336"),sQuery(id+"F13.wireOp",EDGE,"E29.sketch_text.stroke-337"),sQuery(id+"F13.wireOp",EDGE,"E29.sketch_text.stroke-338")])]});
            var Q21;
            Q21=makeQuery(id+"F14.opExtrude","SWEPT_BODY",BODY,{"disambiguationData":[OSD([sQuery(id+"F13.wireOp",EDGE,"E29.sketch_text.stroke-339"),sQuery(id+"F13.wireOp",EDGE,"E29.sketch_text.stroke-340"),sQuery(id+"F13.wireOp",EDGE,"E29.sketch_text.stroke-341"),sQuery(id+"F13.wireOp",EDGE,"E29.sketch_text.stroke-342"),sQuery(id+"F13.wireOp",EDGE,"E29.sketch_text.stroke-343"),sQuery(id+"F13.wireOp",EDGE,"E29.sketch_text.stroke-344"),sQuery(id+"F13.wireOp",EDGE,"E29.sketch_text.stroke-345"),sQuery(id+"F13.wireOp",EDGE,"E29.sketch_text.stroke-346"),sQuery(id+"F13.wireOp",EDGE,"E29.sketch_text.stroke-347"),sQuery(id+"F13.wireOp",EDGE,"E29.sketch_text.stroke-348"),sQuery(id+"F13.wireOp",EDGE,"E29.sketch_text.stroke-349"),sQuery(id+"F13.wireOp",EDGE,"E29.sketch_text.stroke-350"),sQuery(id+"F13.wireOp",EDGE,"E29.sketch_text.stroke-351"),sQuery(id+"F13.wireOp",EDGE,"E29.sketch_text.stroke-352"),sQuery(id+"F13.wireOp",EDGE,"E29.sketch_text.stroke-353"),sQuery(id+"F13.wireOp",EDGE,"E29.sketch_text.stroke-354"),sQuery(id+"F13.wireOp",EDGE,"E29.sketch_text.stroke-355"),sQuery(id+"F13.wireOp",EDGE,"E29.sketch_text.stroke-356"),sQuery(id+"F13.wireOp",EDGE,"E29.sketch_text.stroke-357"),sQuery(id+"F13.wireOp",EDGE,"E29.sketch_text.stroke-358"),sQuery(id+"F13.wireOp",EDGE,"E29.sketch_text.stroke-359"),sQuery(id+"F13.wireOp",EDGE,"E29.sketch_text.stroke-360"),sQuery(id+"F13.wireOp",EDGE,"E29.sketch_text.stroke-361"),sQuery(id+"F13.wireOp",EDGE,"E29.sketch_text.stroke-362"),sQuery(id+"F13.wireOp",EDGE,"E29.sketch_text.stroke-363"),sQuery(id+"F13.wireOp",EDGE,"E29.sketch_text.stroke-364"),sQuery(id+"F13.wireOp",EDGE,"E29.sketch_text.stroke-365"),sQuery(id+"F13.wireOp",EDGE,"E29.sketch_text.stroke-366"),sQuery(id+"F13.wireOp",EDGE,"E29.sketch_text.stroke-367"),sQuery(id+"F13.wireOp",EDGE,"E29.sketch_text.stroke-368"),sQuery(id+"F13.wireOp",EDGE,"E29.sketch_text.stroke-369"),sQuery(id+"F13.wireOp",EDGE,"E29.sketch_text.stroke-370"),sQuery(id+"F13.wireOp",EDGE,"E29.sketch_text.stroke-371"),sQuery(id+"F13.wireOp",EDGE,"E29.sketch_text.stroke-372"),sQuery(id+"F13.wireOp",EDGE,"E29.sketch_text.stroke-373"),sQuery(id+"F13.wireOp",EDGE,"E29.sketch_text.stroke-374"),sQuery(id+"F13.wireOp",EDGE,"E29.sketch_text.stroke-375"),sQuery(id+"F13.wireOp",EDGE,"E29.sketch_text.stroke-376"),sQuery(id+"F13.wireOp",EDGE,"E29.sketch_text.stroke-377"),sQuery(id+"F13.wireOp",EDGE,"E29.sketch_text.stroke-378"),sQuery(id+"F13.wireOp",EDGE,"E29.sketch_text.stroke-379"),sQuery(id+"F13.wireOp",EDGE,"E29.sketch_text.stroke-380"),sQuery(id+"F13.wireOp",EDGE,"E29.sketch_text.stroke-381"),sQuery(id+"F13.wireOp",EDGE,"E29.sketch_text.stroke-382")])]});
            var Q22;
            Q22=makeQuery(id+"F1.opExtrude","SWEPT_BODY",BODY,{"disambiguationData":[OSD([sQuery(id+"F0.wireOp",EDGE,"E0.bottom"),sQuery(id+"F0.wireOp",EDGE,"E0.top"),sQuery(id+"F0.wireOp",EDGE,"E1"),sQuery(id+"F0.wireOp",EDGE,"E2")])]});
            booleanBodies(context, id + "F20", {"operationType" : BooleanOperationType.SUBTRACTION, "tools" : qUnion([Q0, Q1, Q2, Q3, Q4, Q5, Q6, Q7, Q8, Q9, Q10, Q11, Q12, Q13, Q14, Q15, Q16, Q17, Q18, Q19, Q20, Q21]), "targets" : qUnion([Q22]), "keepTools" : true});
        }
        {
            var Q0;
            Q0=makeQuery(id+"F16.opExtrude","SWEPT_BODY",BODY,{"disambiguationData":[OSD([sQuery(id+"F15.wireOp",EDGE,"E30.sketch_text.stroke-0"),sQuery(id+"F15.wireOp",EDGE,"E30.sketch_text.stroke-1"),sQuery(id+"F15.wireOp",EDGE,"E30.sketch_text.stroke-2"),sQuery(id+"F15.wireOp",EDGE,"E30.sketch_text.stroke-3"),sQuery(id+"F15.wireOp",EDGE,"E30.sketch_text.stroke-4"),sQuery(id+"F15.wireOp",EDGE,"E30.sketch_text.stroke-5"),sQuery(id+"F15.wireOp",EDGE,"E30.sketch_text.stroke-6"),sQuery(id+"F15.wireOp",EDGE,"E30.sketch_text.stroke-7"),sQuery(id+"F15.wireOp",EDGE,"E30.sketch_text.stroke-8"),sQuery(id+"F15.wireOp",EDGE,"E30.sketch_text.stroke-9")])]});
            var Q1;
            Q1=makeQuery(id+"F16.opExtrude","SWEPT_BODY",BODY,{"disambiguationData":[OSD([sQuery(id+"F15.wireOp",EDGE,"E30.sketch_text.stroke-10"),sQuery(id+"F15.wireOp",EDGE,"E30.sketch_text.stroke-11"),sQuery(id+"F15.wireOp",EDGE,"E30.sketch_text.stroke-12"),sQuery(id+"F15.wireOp",EDGE,"E30.sketch_text.stroke-13"),sQuery(id+"F15.wireOp",EDGE,"E30.sketch_text.stroke-14"),sQuery(id+"F15.wireOp",EDGE,"E30.sketch_text.stroke-15"),sQuery(id+"F15.wireOp",EDGE,"E30.sketch_text.stroke-16"),sQuery(id+"F15.wireOp",EDGE,"E30.sketch_text.stroke-17"),sQuery(id+"F15.wireOp",EDGE,"E30.sketch_text.stroke-18"),sQuery(id+"F15.wireOp",EDGE,"E30.sketch_text.stroke-19"),sQuery(id+"F15.wireOp",EDGE,"E30.sketch_text.stroke-20"),sQuery(id+"F15.wireOp",EDGE,"E30.sketch_text.stroke-21"),sQuery(id+"F15.wireOp",EDGE,"E30.sketch_text.stroke-22"),sQuery(id+"F15.wireOp",EDGE,"E30.sketch_text.stroke-23"),sQuery(id+"F15.wireOp",EDGE,"E30.sketch_text.stroke-24"),sQuery(id+"F15.wireOp",EDGE,"E30.sketch_text.stroke-25"),sQuery(id+"F15.wireOp",EDGE,"E30.sketch_text.stroke-26"),sQuery(id+"F15.wireOp",EDGE,"E30.sketch_text.stroke-27"),sQuery(id+"F15.wireOp",EDGE,"E30.sketch_text.stroke-28"),sQuery(id+"F15.wireOp",EDGE,"E30.sketch_text.stroke-29"),sQuery(id+"F15.wireOp",EDGE,"E30.sketch_text.stroke-30"),sQuery(id+"F15.wireOp",EDGE,"E30.sketch_text.stroke-31"),sQuery(id+"F15.wireOp",EDGE,"E30.sketch_text.stroke-32"),sQuery(id+"F15.wireOp",EDGE,"E30.sketch_text.stroke-33"),sQuery(id+"F15.wireOp",EDGE,"E30.sketch_text.stroke-34")])]});
            var Q2;
            Q2=makeQuery(id+"F16.opExtrude","SWEPT_BODY",BODY,{"disambiguationData":[OSD([sQuery(id+"F15.wireOp",EDGE,"E30.sketch_text.stroke-35"),sQuery(id+"F15.wireOp",EDGE,"E30.sketch_text.stroke-36"),sQuery(id+"F15.wireOp",EDGE,"E30.sketch_text.stroke-37"),sQuery(id+"F15.wireOp",EDGE,"E30.sketch_text.stroke-38"),sQuery(id+"F15.wireOp",EDGE,"E30.sketch_text.stroke-39"),sQuery(id+"F15.wireOp",EDGE,"E30.sketch_text.stroke-40"),sQuery(id+"F15.wireOp",EDGE,"E30.sketch_text.stroke-41"),sQuery(id+"F15.wireOp",EDGE,"E30.sketch_text.stroke-42"),sQuery(id+"F15.wireOp",EDGE,"E30.sketch_text.stroke-43"),sQuery(id+"F15.wireOp",EDGE,"E30.sketch_text.stroke-44"),sQuery(id+"F15.wireOp",EDGE,"E30.sketch_text.stroke-45"),sQuery(id+"F15.wireOp",EDGE,"E30.sketch_text.stroke-46"),sQuery(id+"F15.wireOp",EDGE,"E30.sketch_text.stroke-47"),sQuery(id+"F15.wireOp",EDGE,"E30.sketch_text.stroke-48"),sQuery(id+"F15.wireOp",EDGE,"E30.sketch_text.stroke-49"),sQuery(id+"F15.wireOp",EDGE,"E30.sketch_text.stroke-50"),sQuery(id+"F15.wireOp",EDGE,"E30.sketch_text.stroke-51"),sQuery(id+"F15.wireOp",EDGE,"E30.sketch_text.stroke-52"),sQuery(id+"F15.wireOp",EDGE,"E30.sketch_text.stroke-53"),sQuery(id+"F15.wireOp",EDGE,"E30.sketch_text.stroke-54"),sQuery(id+"F15.wireOp",EDGE,"E30.sketch_text.stroke-55"),sQuery(id+"F15.wireOp",EDGE,"E30.sketch_text.stroke-56"),sQuery(id+"F15.wireOp",EDGE,"E30.sketch_text.stroke-57"),sQuery(id+"F15.wireOp",EDGE,"E30.sketch_text.stroke-58"),sQuery(id+"F15.wireOp",EDGE,"E30.sketch_text.stroke-59"),sQuery(id+"F15.wireOp",EDGE,"E30.sketch_text.stroke-60"),sQuery(id+"F15.wireOp",EDGE,"E30.sketch_text.stroke-61")])]});
            var Q3;
            Q3=makeQuery(id+"F16.opExtrude","SWEPT_BODY",BODY,{"disambiguationData":[OSD([sQuery(id+"F15.wireOp",EDGE,"E30.sketch_text.stroke-62"),sQuery(id+"F15.wireOp",EDGE,"E30.sketch_text.stroke-63"),sQuery(id+"F15.wireOp",EDGE,"E30.sketch_text.stroke-64"),sQuery(id+"F15.wireOp",EDGE,"E30.sketch_text.stroke-65"),sQuery(id+"F15.wireOp",EDGE,"E30.sketch_text.stroke-66"),sQuery(id+"F15.wireOp",EDGE,"E30.sketch_text.stroke-67"),sQuery(id+"F15.wireOp",EDGE,"E30.sketch_text.stroke-68"),sQuery(id+"F15.wireOp",EDGE,"E30.sketch_text.stroke-69"),sQuery(id+"F15.wireOp",EDGE,"E30.sketch_text.stroke-70"),sQuery(id+"F15.wireOp",EDGE,"E30.sketch_text.stroke-71")])]});
            var Q4;
            Q4=makeQuery(id+"F16.opExtrude","SWEPT_BODY",BODY,{"disambiguationData":[OSD([sQuery(id+"F15.wireOp",EDGE,"E30.sketch_text.stroke-72"),sQuery(id+"F15.wireOp",EDGE,"E30.sketch_text.stroke-73"),sQuery(id+"F15.wireOp",EDGE,"E30.sketch_text.stroke-74"),sQuery(id+"F15.wireOp",EDGE,"E30.sketch_text.stroke-75"),sQuery(id+"F15.wireOp",EDGE,"E30.sketch_text.stroke-76"),sQuery(id+"F15.wireOp",EDGE,"E30.sketch_text.stroke-77"),sQuery(id+"F15.wireOp",EDGE,"E30.sketch_text.stroke-78"),sQuery(id+"F15.wireOp",EDGE,"E30.sketch_text.stroke-79"),sQuery(id+"F15.wireOp",EDGE,"E30.sketch_text.stroke-80"),sQuery(id+"F15.wireOp",EDGE,"E30.sketch_text.stroke-81")])]});
            var Q5;
            Q5=makeQuery(id+"F16.opExtrude","SWEPT_BODY",BODY,{"disambiguationData":[OSD([sQuery(id+"F15.wireOp",EDGE,"E30.sketch_text.stroke-82"),sQuery(id+"F15.wireOp",EDGE,"E30.sketch_text.stroke-83"),sQuery(id+"F15.wireOp",EDGE,"E30.sketch_text.stroke-84"),sQuery(id+"F15.wireOp",EDGE,"E30.sketch_text.stroke-85"),sQuery(id+"F15.wireOp",EDGE,"E30.sketch_text.stroke-86"),sQuery(id+"F15.wireOp",EDGE,"E30.sketch_text.stroke-87"),sQuery(id+"F15.wireOp",EDGE,"E30.sketch_text.stroke-88"),sQuery(id+"F15.wireOp",EDGE,"E30.sketch_text.stroke-89"),sQuery(id+"F15.wireOp",EDGE,"E30.sketch_text.stroke-90"),sQuery(id+"F15.wireOp",EDGE,"E30.sketch_text.stroke-91"),sQuery(id+"F15.wireOp",EDGE,"E30.sketch_text.stroke-92"),sQuery(id+"F15.wireOp",EDGE,"E30.sketch_text.stroke-93"),sQuery(id+"F15.wireOp",EDGE,"E30.sketch_text.stroke-94"),sQuery(id+"F15.wireOp",EDGE,"E30.sketch_text.stroke-95"),sQuery(id+"F15.wireOp",EDGE,"E30.sketch_text.stroke-96"),sQuery(id+"F15.wireOp",EDGE,"E30.sketch_text.stroke-97"),sQuery(id+"F15.wireOp",EDGE,"E30.sketch_text.stroke-98"),sQuery(id+"F15.wireOp",EDGE,"E30.sketch_text.stroke-99"),sQuery(id+"F15.wireOp",EDGE,"E30.sketch_text.stroke-100"),sQuery(id+"F15.wireOp",EDGE,"E30.sketch_text.stroke-101"),sQuery(id+"F15.wireOp",EDGE,"E30.sketch_text.stroke-102"),sQuery(id+"F15.wireOp",EDGE,"E30.sketch_text.stroke-103"),sQuery(id+"F15.wireOp",EDGE,"E30.sketch_text.stroke-104"),sQuery(id+"F15.wireOp",EDGE,"E30.sketch_text.stroke-105"),sQuery(id+"F15.wireOp",EDGE,"E30.sketch_text.stroke-106"),sQuery(id+"F15.wireOp",EDGE,"E30.sketch_text.stroke-107"),sQuery(id+"F15.wireOp",EDGE,"E30.sketch_text.stroke-108")])]});
            var Q6;
            Q6=makeQuery(id+"F16.opExtrude","SWEPT_BODY",BODY,{"disambiguationData":[OSD([sQuery(id+"F15.wireOp",EDGE,"E30.sketch_text.stroke-109"),sQuery(id+"F15.wireOp",EDGE,"E30.sketch_text.stroke-110"),sQuery(id+"F15.wireOp",EDGE,"E30.sketch_text.stroke-111"),sQuery(id+"F15.wireOp",EDGE,"E30.sketch_text.stroke-112"),sQuery(id+"F15.wireOp",EDGE,"E30.sketch_text.stroke-113"),sQuery(id+"F15.wireOp",EDGE,"E30.sketch_text.stroke-114"),sQuery(id+"F15.wireOp",EDGE,"E30.sketch_text.stroke-115"),sQuery(id+"F15.wireOp",EDGE,"E30.sketch_text.stroke-116"),sQuery(id+"F15.wireOp",EDGE,"E30.sketch_text.stroke-117"),sQuery(id+"F15.wireOp",EDGE,"E30.sketch_text.stroke-118"),sQuery(id+"F15.wireOp",EDGE,"E30.sketch_text.stroke-119"),sQuery(id+"F15.wireOp",EDGE,"E30.sketch_text.stroke-120"),sQuery(id+"F15.wireOp",EDGE,"E30.sketch_text.stroke-121"),sQuery(id+"F15.wireOp",EDGE,"E30.sketch_text.stroke-122"),sQuery(id+"F15.wireOp",EDGE,"E30.sketch_text.stroke-123"),sQuery(id+"F15.wireOp",EDGE,"E30.sketch_text.stroke-124"),sQuery(id+"F15.wireOp",EDGE,"E30.sketch_text.stroke-125"),sQuery(id+"F15.wireOp",EDGE,"E30.sketch_text.stroke-126"),sQuery(id+"F15.wireOp",EDGE,"E30.sketch_text.stroke-127"),sQuery(id+"F15.wireOp",EDGE,"E30.sketch_text.stroke-128"),sQuery(id+"F15.wireOp",EDGE,"E30.sketch_text.stroke-129"),sQuery(id+"F15.wireOp",EDGE,"E30.sketch_text.stroke-130"),sQuery(id+"F15.wireOp",EDGE,"E30.sketch_text.stroke-131"),sQuery(id+"F15.wireOp",EDGE,"E30.sketch_text.stroke-132"),sQuery(id+"F15.wireOp",EDGE,"E30.sketch_text.stroke-133")])]});
            var Q7;
            Q7=makeQuery(id+"F16.opExtrude","SWEPT_BODY",BODY,{"disambiguationData":[OSD([sQuery(id+"F15.wireOp",EDGE,"E30.sketch_text.stroke-134"),sQuery(id+"F15.wireOp",EDGE,"E30.sketch_text.stroke-135"),sQuery(id+"F15.wireOp",EDGE,"E30.sketch_text.stroke-136"),sQuery(id+"F15.wireOp",EDGE,"E30.sketch_text.stroke-137"),sQuery(id+"F15.wireOp",EDGE,"E30.sketch_text.stroke-138"),sQuery(id+"F15.wireOp",EDGE,"E30.sketch_text.stroke-139"),sQuery(id+"F15.wireOp",EDGE,"E30.sketch_text.stroke-140"),sQuery(id+"F15.wireOp",EDGE,"E30.sketch_text.stroke-141"),sQuery(id+"F15.wireOp",EDGE,"E30.sketch_text.stroke-142"),sQuery(id+"F15.wireOp",EDGE,"E30.sketch_text.stroke-143"),sQuery(id+"F15.wireOp",EDGE,"E30.sketch_text.stroke-144"),sQuery(id+"F15.wireOp",EDGE,"E30.sketch_text.stroke-145"),sQuery(id+"F15.wireOp",EDGE,"E30.sketch_text.stroke-146"),sQuery(id+"F15.wireOp",EDGE,"E30.sketch_text.stroke-147"),sQuery(id+"F15.wireOp",EDGE,"E30.sketch_text.stroke-148"),sQuery(id+"F15.wireOp",EDGE,"E30.sketch_text.stroke-149")])]});
            var Q8;
            Q8=makeQuery(id+"F16.opExtrude","SWEPT_BODY",BODY,{"disambiguationData":[OSD([sQuery(id+"F15.wireOp",EDGE,"E30.sketch_text.stroke-150"),sQuery(id+"F15.wireOp",EDGE,"E30.sketch_text.stroke-151"),sQuery(id+"F15.wireOp",EDGE,"E30.sketch_text.stroke-152"),sQuery(id+"F15.wireOp",EDGE,"E30.sketch_text.stroke-153")])]});
            var Q9;
            Q9=makeQuery(id+"F16.opExtrude","SWEPT_BODY",BODY,{"disambiguationData":[OSD([sQuery(id+"F15.wireOp",EDGE,"E30.sketch_text.stroke-154"),sQuery(id+"F15.wireOp",EDGE,"E30.sketch_text.stroke-155"),sQuery(id+"F15.wireOp",EDGE,"E30.sketch_text.stroke-156"),sQuery(id+"F15.wireOp",EDGE,"E30.sketch_text.stroke-157"),sQuery(id+"F15.wireOp",EDGE,"E30.sketch_text.stroke-158"),sQuery(id+"F15.wireOp",EDGE,"E30.sketch_text.stroke-159"),sQuery(id+"F15.wireOp",EDGE,"E30.sketch_text.stroke-160"),sQuery(id+"F15.wireOp",EDGE,"E30.sketch_text.stroke-161"),sQuery(id+"F15.wireOp",EDGE,"E30.sketch_text.stroke-162"),sQuery(id+"F15.wireOp",EDGE,"E30.sketch_text.stroke-163")])]});
            var Q10;
            Q10=makeQuery(id+"F16.opExtrude","SWEPT_BODY",BODY,{"disambiguationData":[OSD([sQuery(id+"F15.wireOp",EDGE,"E30.sketch_text.stroke-164"),sQuery(id+"F15.wireOp",EDGE,"E30.sketch_text.stroke-165"),sQuery(id+"F15.wireOp",EDGE,"E30.sketch_text.stroke-166"),sQuery(id+"F15.wireOp",EDGE,"E30.sketch_text.stroke-167"),sQuery(id+"F15.wireOp",EDGE,"E30.sketch_text.stroke-168"),sQuery(id+"F15.wireOp",EDGE,"E30.sketch_text.stroke-169"),sQuery(id+"F15.wireOp",EDGE,"E30.sketch_text.stroke-170"),sQuery(id+"F15.wireOp",EDGE,"E30.sketch_text.stroke-171"),sQuery(id+"F15.wireOp",EDGE,"E30.sketch_text.stroke-172"),sQuery(id+"F15.wireOp",EDGE,"E30.sketch_text.stroke-173"),sQuery(id+"F15.wireOp",EDGE,"E30.sketch_text.stroke-174"),sQuery(id+"F15.wireOp",EDGE,"E30.sketch_text.stroke-175"),sQuery(id+"F15.wireOp",EDGE,"E30.sketch_text.stroke-176"),sQuery(id+"F15.wireOp",EDGE,"E30.sketch_text.stroke-177"),sQuery(id+"F15.wireOp",EDGE,"E30.sketch_text.stroke-178"),sQuery(id+"F15.wireOp",EDGE,"E30.sketch_text.stroke-179"),sQuery(id+"F15.wireOp",EDGE,"E30.sketch_text.stroke-180"),sQuery(id+"F15.wireOp",EDGE,"E30.sketch_text.stroke-181"),sQuery(id+"F15.wireOp",EDGE,"E30.sketch_text.stroke-182"),sQuery(id+"F15.wireOp",EDGE,"E30.sketch_text.stroke-183"),sQuery(id+"F15.wireOp",EDGE,"E30.sketch_text.stroke-184"),sQuery(id+"F15.wireOp",EDGE,"E30.sketch_text.stroke-185"),sQuery(id+"F15.wireOp",EDGE,"E30.sketch_text.stroke-186"),sQuery(id+"F15.wireOp",EDGE,"E30.sketch_text.stroke-187")])]});
            var Q11;
            Q11=makeQuery(id+"F16.opExtrude","SWEPT_BODY",BODY,{"disambiguationData":[OSD([sQuery(id+"F15.wireOp",EDGE,"E30.sketch_text.stroke-188"),sQuery(id+"F15.wireOp",EDGE,"E30.sketch_text.stroke-189"),sQuery(id+"F15.wireOp",EDGE,"E30.sketch_text.stroke-190"),sQuery(id+"F15.wireOp",EDGE,"E30.sketch_text.stroke-191"),sQuery(id+"F15.wireOp",EDGE,"E30.sketch_text.stroke-192"),sQuery(id+"F15.wireOp",EDGE,"E30.sketch_text.stroke-193"),sQuery(id+"F15.wireOp",EDGE,"E30.sketch_text.stroke-194"),sQuery(id+"F15.wireOp",EDGE,"E30.sketch_text.stroke-195"),sQuery(id+"F15.wireOp",EDGE,"E30.sketch_text.stroke-196"),sQuery(id+"F15.wireOp",EDGE,"E30.sketch_text.stroke-197"),sQuery(id+"F15.wireOp",EDGE,"E30.sketch_text.stroke-198"),sQuery(id+"F15.wireOp",EDGE,"E30.sketch_text.stroke-199"),sQuery(id+"F15.wireOp",EDGE,"E30.sketch_text.stroke-200"),sQuery(id+"F15.wireOp",EDGE,"E30.sketch_text.stroke-201"),sQuery(id+"F15.wireOp",EDGE,"E30.sketch_text.stroke-202"),sQuery(id+"F15.wireOp",EDGE,"E30.sketch_text.stroke-203")])]});
            var Q12;
            Q12=makeQuery(id+"F16.opExtrude","SWEPT_BODY",BODY,{"disambiguationData":[OSD([sQuery(id+"F15.wireOp",EDGE,"E30.sketch_text.stroke-204"),sQuery(id+"F15.wireOp",EDGE,"E30.sketch_text.stroke-205"),sQuery(id+"F15.wireOp",EDGE,"E30.sketch_text.stroke-206"),sQuery(id+"F15.wireOp",EDGE,"E30.sketch_text.stroke-207"),sQuery(id+"F15.wireOp",EDGE,"E30.sketch_text.stroke-208"),sQuery(id+"F15.wireOp",EDGE,"E30.sketch_text.stroke-209"),sQuery(id+"F15.wireOp",EDGE,"E30.sketch_text.stroke-210"),sQuery(id+"F15.wireOp",EDGE,"E30.sketch_text.stroke-211"),sQuery(id+"F15.wireOp",EDGE,"E30.sketch_text.stroke-212"),sQuery(id+"F15.wireOp",EDGE,"E30.sketch_text.stroke-213"),sQuery(id+"F15.wireOp",EDGE,"E30.sketch_text.stroke-214"),sQuery(id+"F15.wireOp",EDGE,"E30.sketch_text.stroke-215"),sQuery(id+"F15.wireOp",EDGE,"E30.sketch_text.stroke-216"),sQuery(id+"F15.wireOp",EDGE,"E30.sketch_text.stroke-217"),sQuery(id+"F15.wireOp",EDGE,"E30.sketch_text.stroke-218"),sQuery(id+"F15.wireOp",EDGE,"E30.sketch_text.stroke-219"),sQuery(id+"F15.wireOp",EDGE,"E30.sketch_text.stroke-220"),sQuery(id+"F15.wireOp",EDGE,"E30.sketch_text.stroke-221"),sQuery(id+"F15.wireOp",EDGE,"E30.sketch_text.stroke-222"),sQuery(id+"F15.wireOp",EDGE,"E30.sketch_text.stroke-223"),sQuery(id+"F15.wireOp",EDGE,"E30.sketch_text.stroke-224"),sQuery(id+"F15.wireOp",EDGE,"E30.sketch_text.stroke-225"),sQuery(id+"F15.wireOp",EDGE,"E30.sketch_text.stroke-226"),sQuery(id+"F15.wireOp",EDGE,"E30.sketch_text.stroke-227"),sQuery(id+"F15.wireOp",EDGE,"E30.sketch_text.stroke-228"),sQuery(id+"F15.wireOp",EDGE,"E30.sketch_text.stroke-229"),sQuery(id+"F15.wireOp",EDGE,"E30.sketch_text.stroke-230"),sQuery(id+"F15.wireOp",EDGE,"E30.sketch_text.stroke-231"),sQuery(id+"F15.wireOp",EDGE,"E30.sketch_text.stroke-232"),sQuery(id+"F15.wireOp",EDGE,"E30.sketch_text.stroke-233"),sQuery(id+"F15.wireOp",EDGE,"E30.sketch_text.stroke-234")])]});
            var Q13;
            Q13=makeQuery(id+"F1.opExtrude","SWEPT_BODY",BODY,{"disambiguationData":[OSD([sQuery(id+"F0.wireOp",EDGE,"E0.bottom"),sQuery(id+"F0.wireOp",EDGE,"E0.top"),sQuery(id+"F0.wireOp",EDGE,"E1"),sQuery(id+"F0.wireOp",EDGE,"E2")])]});
            booleanBodies(context, id + "F21", {"operationType" : BooleanOperationType.SUBTRACTION, "tools" : qUnion([Q0, Q1, Q2, Q3, Q4, Q5, Q6, Q7, Q8, Q9, Q10, Q11, Q12]), "targets" : qUnion([Q13]), "keepTools" : true});
        }
        {
            var Q0;
            Q0=makeQuery(id+"F10.opExtrude","SWEPT_BODY",BODY,{"disambiguationData":[OSD([sQuery(id+"F9.wireOp",EDGE,"E27.1.0")])]});
            var Q1;
            Q1=makeQuery(id+"F1.opExtrude","SWEPT_BODY",BODY,{"disambiguationData":[OSD([sQuery(id+"F0.wireOp",EDGE,"E0.bottom"),sQuery(id+"F0.wireOp",EDGE,"E0.top"),sQuery(id+"F0.wireOp",EDGE,"E1"),sQuery(id+"F0.wireOp",EDGE,"E2")])]});
            booleanBodies(context, id + "F22", {"operationType" : BooleanOperationType.SUBTRACTION, "tools" : qUnion([Q0]), "targets" : qUnion([Q1]), "keepTools" : true});
        }
        {
            var Q0;
            Q0=qCreatedBy(makeId("Top.planeOp"),FACE);
            var sketch = newSketch(context, id + "F23", { "sketchPlane" : qUnion([Q0])});
            skCircle(sketch, "E31", {"center": v(-48, 0) * mm, "radius": 1.63 * mm});
            skCircle(sketch, "E32.MirrorC", {"center": v(48, 0) * mm, "radius": 1.63 * mm});
            skSolve(sketch);
        }
        {
            var Q0;
            Q0=qSketchRegion(id+"F23",true);
            extrude(context, id + "F24", {"entities" : qUnion([Q0]), "operationType" : NewBodyOperationType.REMOVE, "endBound" : BoundingType.THROUGH_ALL, "depth" : 25 * mm});
        }
        {
            var Q0;
            Q0=makeQuery(id+"F4.opExtrude","SWEPT_BODY",BODY,{"disambiguationData":[OSD([sQuery(id+"F3.wireOp",EDGE,"E3"),sQuery(id+"F3.wireOp",EDGE,"E4.0"),sQuery(id+"F3.wireOp",EDGE,"E5.MirrorC"),sQuery(id+"F3.wireOp",EDGE,"E6.MirrorC"),sQuery(id+"F3.wireOp",EDGE,"E7"),sQuery(id+"F3.wireOp",EDGE,"E8.MirrorCS"),sQuery(id+"F3.wireOp",EDGE,"E9.0"),sQuery(id+"F3.wireOp",EDGE,"E10.MirrorCS")])]});
            var Q1;
            Q1=makeQuery(id+"F1.opExtrude","SWEPT_BODY",BODY,{"disambiguationData":[OSD([sQuery(id+"F0.wireOp",EDGE,"E0.bottom"),sQuery(id+"F0.wireOp",EDGE,"E0.top"),sQuery(id+"F0.wireOp",EDGE,"E1"),sQuery(id+"F0.wireOp",EDGE,"E2")])]});
            booleanBodies(context, id + "F25", {"operationType" : BooleanOperationType.SUBTRACTION, "tools" : qUnion([Q0]), "targets" : qUnion([Q1]), "keepTools" : true});
        }
    });
